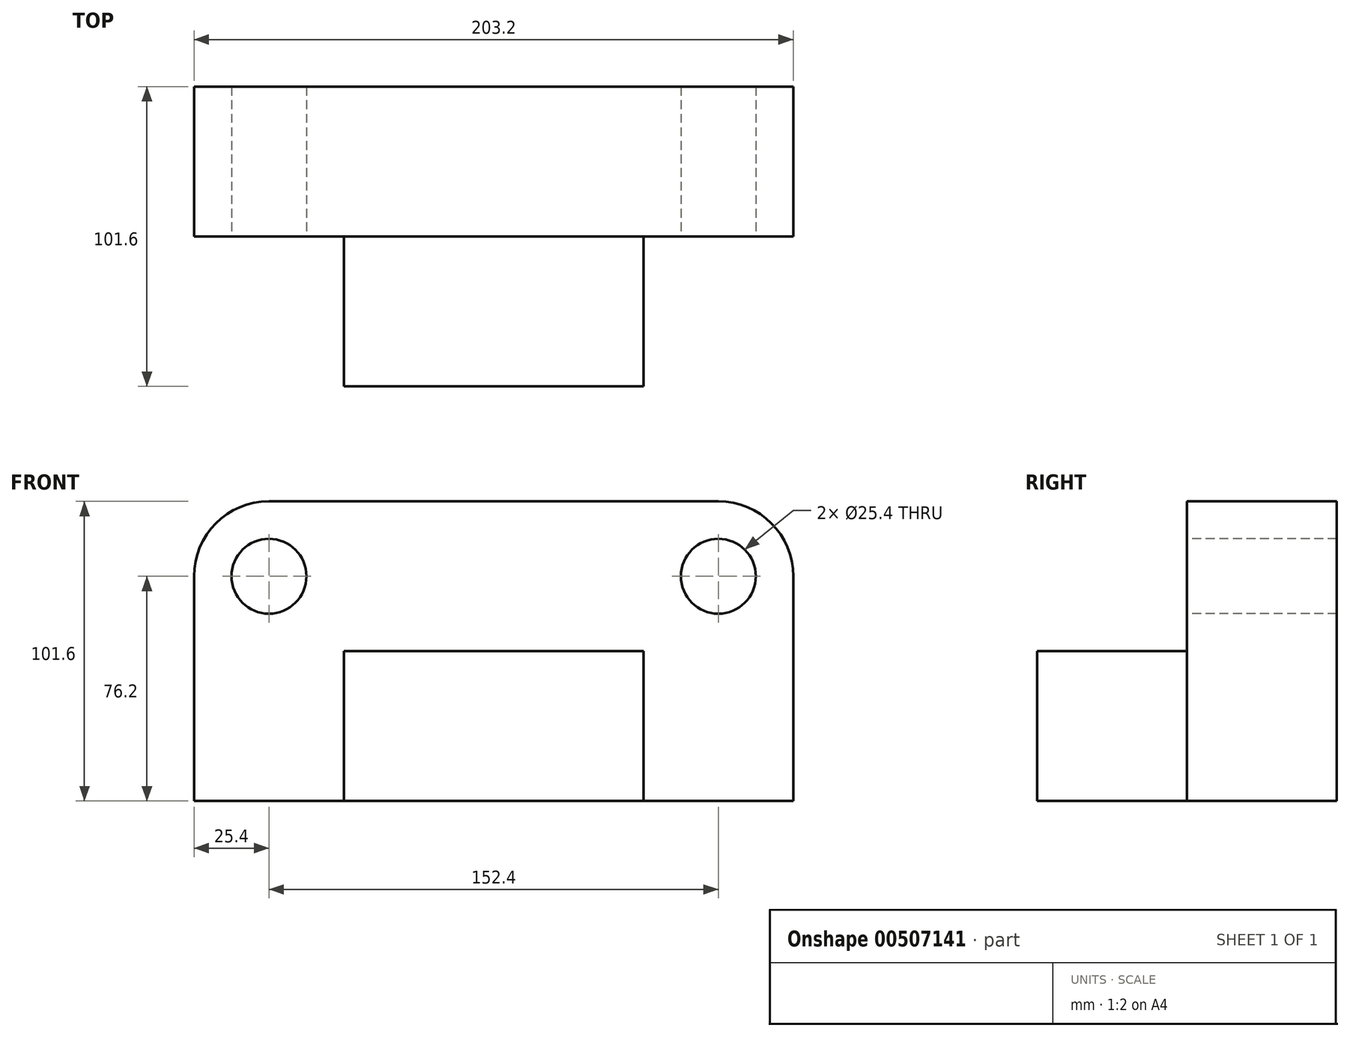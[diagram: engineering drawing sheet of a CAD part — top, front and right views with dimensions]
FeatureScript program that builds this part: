
annotation { "Feature Type Name" : "Feature", "Feature Type Description" : "" }
export const myFeature = defineFeature(function(context is Context, id is Id, definition is map)
    precondition{}
    {
        {
            var Q0;
            Q0=qCreatedBy(makeId("Front.planeOp"),FACE);
            var sketch = newSketch(context, id + "F0", { "sketchPlane" : qUnion([Q0])});
            skLineSegment(sketch, "E0.bottom", {"start": v(-101.6, 50.8) * mm, "end": v(101.6, 50.8) * mm});
            skLineSegment(sketch, "E0.top", {"start": v(-101.6, -50.8) * mm, "end": v(101.6, -50.8) * mm});
            skLineSegment(sketch, "E0.left", {"start": v(-101.6, 50.8) * mm, "end": v(-101.6, -50.8) * mm});
            skLineSegment(sketch, "E0.right", {"start": v(101.6, 50.8) * mm, "end": v(101.6, -50.8) * mm});
            skPoint(sketch, "E0.middle", {"position": v(0, 0) * mm});
            skLineSegment(sketch, "E1.bottom", {"start": v(101.6, -50.8) * mm, "end": v(50.8, -50.8) * mm});
            skLineSegment(sketch, "E1.top", {"start": v(101.6, 0) * mm, "end": v(50.8, 0) * mm});
            skLineSegment(sketch, "E1.left", {"start": v(101.6, -50.8) * mm, "end": v(101.6, 0) * mm});
            skLineSegment(sketch, "E1.right", {"start": v(50.8, -50.8) * mm, "end": v(50.8, 0) * mm});
            skLineSegment(sketch, "E2.bottom", {"start": v(-101.6, -50.8) * mm, "end": v(-50.8, -50.8) * mm});
            skLineSegment(sketch, "E2.top", {"start": v(-101.6, 0) * mm, "end": v(-50.8, 0) * mm});
            skLineSegment(sketch, "E2.left", {"start": v(-101.6, -50.8) * mm, "end": v(-101.6, 0) * mm});
            skLineSegment(sketch, "E2.right", {"start": v(-50.8, -50.8) * mm, "end": v(-50.8, 0) * mm});
            skLineSegment(sketch, "E3.bottom", {"start": v(-101.6, 0) * mm, "end": v(101.6, 0) * mm});
            skLineSegment(sketch, "E3.top", {"start": v(-101.6, 0) * mm, "end": v(101.6, 0) * mm});
            skLineSegment(sketch, "E3.left", {"start": v(-101.6, 0) * mm, "end": v(-101.6, 0) * mm});
            skLineSegment(sketch, "E3.right", {"start": v(101.6, 0) * mm, "end": v(101.6, 0) * mm});
            skSolve(sketch);
        }
        {
            var Q0;
            Q0=makeQuery(id+"F0.imprint","IMPRINT",FACE,{"disambiguationData":[TD([[makeQuery(id+"F0.imprint","IMPRINT",EDGE,{"derivedFrom":sQuery(id+"F0.wireOp",EDGE,"E0.top")}),1.0]])]});
            var Q1;
            Q1=makeQuery(id+"F0.imprint","IMPRINT",FACE,{"disambiguationData":[TD([[makeQuery(id+"F0.imprint","IMPRINT",EDGE,{"derivedFrom":sQuery(id+"F0.wireOp",EDGE,"E0.bottom")}),-1.0]])]});
            extrude(context, id + "F1", {"entities" : qUnion([Q0, Q1]), "depth" : 25.4 * mm});
        }
        {
            var Q0;
            Q0=makeQuery(id+"F1.opExtrude","CAP_FACE",FACE,{"disambiguationData":[OSD([sQuery(id+"F0.wireOp",EDGE,"E0.bottom"),sQuery(id+"F0.wireOp",EDGE,"E0.left"),sQuery(id+"F0.wireOp",EDGE,"E0.right"),sQuery(id+"F0.wireOp",EDGE,"E3.bottom")])],"isStart":true});
            var sketch = newSketch(context, id + "F2", { "sketchPlane" : qUnion([Q0])});
            skLineSegment(sketch, "E4.bottom", {"start": v(-101.6, 50.8) * mm, "end": v(101.6, 50.8) * mm});
            skLineSegment(sketch, "E4.top", {"start": v(-101.6, -50.8) * mm, "end": v(101.6, -50.8) * mm});
            skLineSegment(sketch, "E4.left", {"start": v(-101.6, 50.8) * mm, "end": v(-101.6, -50.8) * mm});
            skLineSegment(sketch, "E4.right", {"start": v(101.6, 50.8) * mm, "end": v(101.6, -50.8) * mm});
            skSolve(sketch);
        }
        {
            var Q0;
            {var subQ0=sQuery(id+"F2.wireOp",EDGE,"E4.top");Q0=makeQuery(id+"F2.imprint","IMPRINT",FACE,{"disambiguationData":[TD([[makeQuery(id+"F2.imprint","IMPRINT",EDGE,{"derivedFrom":subQ0}),1.0]])]});}
            var Q1;
            {var subQ0=sQuery(id+"F2.wireOp",EDGE,"E4.bottom");Q1=makeQuery(id+"F2.imprint","IMPRINT",FACE,{"disambiguationData":[TD([[makeQuery(id+"F2.imprint","IMPRINT",EDGE,{"derivedFrom":subQ0}),1.0]])]});}
            extrude(context, id + "F3", {"entities" : qUnion([Q0, Q1]), "operationType" : NewBodyOperationType.ADD, "depth" : 25.4 * mm});
        }
        {
            var Q0;
            Q0=makeQuery(id+"F1.opExtrude","SWEPT_EDGE",EDGE,{"disambiguationData":[OSD([sQuery(id+"F0.wireOp",EDGE,"E0.bottom"),sQuery(id+"F0.wireOp",EDGE,"E0.right")])]});
            var Q1;
            Q1=makeQuery(id+"F3.opExtrude","SWEPT_EDGE",EDGE,{"disambiguationData":[OSD([sQuery(id+"F2.wireOp",EDGE,"E4.bottom"),sQuery(id+"F2.wireOp",EDGE,"E4.left")])]});
            fillet(context, id + "F4", {"entities" : qUnion([Q0, Q1]), "radius" : 25.4 * mm, "tangentPropagation" : true, "allowEdgeOverflow" : false});
        }
        {
            var Q0;
            Q0=makeQuery(id+"F3.opExtrude","SWEPT_EDGE",EDGE,{"disambiguationData":[OSD([sQuery(id+"F2.wireOp",EDGE,"E4.bottom"),sQuery(id+"F2.wireOp",EDGE,"E4.right")])]});
            var Q1;
            Q1=makeQuery(id+"F1.opExtrude","SWEPT_EDGE",EDGE,{"disambiguationData":[OSD([sQuery(id+"F0.wireOp",EDGE,"E0.bottom"),sQuery(id+"F0.wireOp",EDGE,"E0.left")])]});
            fillet(context, id + "F5", {"entities" : qUnion([Q0, Q1]), "radius" : 25.4 * mm, "tangentPropagation" : true, "allowEdgeOverflow" : false});
        }
        {
            var Q0;
            Q0=makeQuery(id+"F1.opExtrude","CAP_FACE",FACE,{"disambiguationData":[OSD([sQuery(id+"F0.wireOp",EDGE,"E0.bottom"),sQuery(id+"F0.wireOp",EDGE,"E0.top"),sQuery(id+"F0.wireOp",EDGE,"E0.left"),sQuery(id+"F0.wireOp",EDGE,"E0.right"),sQuery(id+"F0.wireOp",EDGE,"E1.right"),sQuery(id+"F0.wireOp",EDGE,"E2.right"),sQuery(id+"F0.wireOp",EDGE,"E3.top")])],"isStart":false});
            var sketch = newSketch(context, id + "F6", { "sketchPlane" : qUnion([Q0])});
            skLineSegment(sketch, "E5.bottom", {"start": v(-50.8, 0) * mm, "end": v(50.8, 0) * mm});
            skLineSegment(sketch, "E5.top", {"start": v(-50.8, -50.8) * mm, "end": v(50.8, -50.8) * mm});
            skLineSegment(sketch, "E5.left", {"start": v(-50.8, 0) * mm, "end": v(-50.8, -50.8) * mm});
            skLineSegment(sketch, "E5.right", {"start": v(50.8, 0) * mm, "end": v(50.8, -50.8) * mm});
            skCircle(sketch, "E6", {"center": v(76.2, 25.4) * mm, "radius": 12.7 * mm});
            skCircle(sketch, "E7", {"center": v(-76.2, 25.4) * mm, "radius": 12.7 * mm});
            skSolve(sketch);
        }
        {
            var Q0;
            Q0=makeQuery(id+"F6.imprint","IMPRINT",FACE,{"disambiguationData":[TD([[makeQuery(id+"F6.imprint","IMPRINT",EDGE,{"derivedFrom":sQuery(id+"F6.wireOp",EDGE,"E5.bottom")}),-1.0]])]});
            extrude(context, id + "F7", {"entities" : qUnion([Q0]), "operationType" : NewBodyOperationType.ADD, "depth" : 50.8 * mm});
        }
        {
            var Q0;
            Q0=makeQuery(id+"F6.imprint","IMPRINT",FACE,{"disambiguationData":[TD([[makeQuery(id+"F6.imprint","IMPRINT",EDGE,{"derivedFrom":sQuery(id+"F6.wireOp",EDGE,"E7")}),1.0]])]});
            var Q1;
            Q1=makeQuery(id+"F6.imprint","IMPRINT",FACE,{"disambiguationData":[TD([[makeQuery(id+"F6.imprint","IMPRINT",EDGE,{"derivedFrom":sQuery(id+"F6.wireOp",EDGE,"E6")}),1.0]])]});
            var Q2;
            Q2=makeQuery(id+"F3.opExtrude","CAP_FACE",FACE,{"disambiguationData":[OSD([sQuery(id+"F2.wireOp",EDGE,"E4.bottom"),sQuery(id+"F2.wireOp",EDGE,"E4.top"),sQuery(id+"F2.wireOp",EDGE,"E4.left"),sQuery(id+"F2.wireOp",EDGE,"E4.right")])],"isStart":false});
            extrude(context, id + "F8", {"entities" : qUnion([Q0, Q1]), "operationType" : NewBodyOperationType.REMOVE, "endBound" : BoundingType.UP_TO_SURFACE, "oppositeDirection" : true, "endBoundEntityFace" : qUnion([Q2]), "depth" : 50.8 * mm});
        }
    });
